# Revit family: DiLED III - Generic_3
name_source: partatom
category: Lighting Fixtures
revit_build: Autodesk Revit Architecture 2012 (Build: 20110916_2132(x64)
units: mm (PartAtom-declared; Revit-internal decimal feet)

## types (8) — shared parameters
Apparent Load = 240 VA
Assembly Code = D5020200
Cassette = Powdercoated Steel (White)
Clearance Zones Offset = 60.00 mm
Color Filter = 16777215
Dimming Lamp Color Temperature Shift = <None>
Emit Shape Visible in Rendering = No
Frame = Powdercoated Steel (White)
Glass = Lamp Glass (Opal)
Glass Thickness = 2.00 mm
Model = DiLED III
Tilt Angle = 90.00°
Transformer = Powdercoated Steel (White)
URL = www.riegens.co.uk

## per-type parameters (varying)
| type | Cassette Depth | Cassette Thickness | Cassette Width | Clearance Zones | Emit from Rectangle Length | Emit from Rectangle Width | Frame Depth | Frame Thickness | Frame Width | Glass Depth | Glass Width | Manufacturer | Photometric Web File | Transformer Offset 1 | Transformer Offset 2 | Transformer Thickness | Voids Angle |
| 300x300 - 3000K | 276.00 mm | 38.75 mm | 276.00 mm | Yes | 295.00 mm | 295.00 mm | 295.00 mm | 10.00 mm | 295.00 mm | 272.00 mm | 272.00 mm | Riegens Lighting | 8246075684_DiLEDIIIG2600x600TL152442WLED3000KCDOpal-11002.ies | 0.00 mm | 146.80 mm | 38.00 mm | 0.00° |
| 300x1200 - 3000K | 1150.00 mm | 40.20 mm | 274.00 mm | Yes | 1195.00 mm | 295.00 mm | 1195.00 mm | 9.55 mm | 295.00 mm | 1147.00 mm | 247.00 mm | Riegens Ligthing | 8246075684_DiLEDIIIG2600x600TL152442WLED3000KCDOpal-11002.ies | 275.00 mm | 275.00 mm | 36.00 mm | 33.00° |
| 625x625 - 3000K | 550.00 mm | 42.40 mm | 550.00 mm | Yes | 620.00 mm | 620.00 mm | 620.00 mm | 9.60 mm | 620.00 mm | 550.00 mm | 550.00 mm | Riegens Lighting | 8246075684_DiLEDIIIG2600x600TL152442WLED3000KCDOpal-11002.ies | 229.00 mm | 229.00 mm | 42.40 mm | 0.00° |
| 600x600 - 3000K | 550.00 mm | 42.40 mm | 550.00 mm | Yes | 595.00 mm | 595.00 mm | 595.00 mm | 9.60 mm | 595.00 mm | 549.00 mm | 549.00 mm | Riegens Ligthing | 8246075684_DiLEDIIIG2600x600TL152442WLED3000KCDOpal-11002.ies | 228.60 mm | 228.60 mm | 42.40 mm | 0.00° |
| 300x300 - 4000K | 276.00 mm | 38.75 mm | 276.00 mm | Yes | 295.00 mm | 295.00 mm | 295.00 mm | 10.00 mm | 295.00 mm | 272.00 mm | 272.00 mm | Riegens Lighting | 8246075749_DiLEDIIIG2600x600TL152442WLED4000KCDOpal-11016.ies | 0.00 mm | 146.80 mm | 38.00 mm | 0.00° |
| 300x1200 - 4000K | 1150.00 mm | 40.20 mm | 274.00 mm | Yes | 1195.00 mm | 295.00 mm | 1195.00 mm | 9.55 mm | 295.00 mm | 1147.00 mm | 247.00 mm | Riegens Lighting | 8246075749_DiLEDIIIG2600x600TL152442WLED4000KCDOpal-11016.ies | 275.00 mm | 275.00 mm | 36.00 mm | 33.00° |
| 600x600 - 4000K | 550.00 mm | 42.40 mm | 550.00 mm | No | 595.00 mm | 595.00 mm | 595.00 mm | 9.60 mm | 595.00 mm | 549.00 mm | 549.00 mm | Riegens Lighting | 8246075749_DiLEDIIIG2600x600TL152442WLED4000KCDOpal-11016.ies | 228.60 mm | 228.60 mm | 42.40 mm | 0.00° |
| 625x625 - 4000K | 550.00 mm | 42.40 mm | 550.00 mm | Yes | 620.00 mm | 620.00 mm | 620.00 mm | 9.60 mm | 620.00 mm | 550.00 mm | 550.00 mm | Riegens Lighting | 8246075749_DiLEDIIIG2600x600TL152442WLED4000KCDOpal-11016.ies | 229.00 mm | 229.00 mm | 42.40 mm | 0.00° |

## geometry (parser evidence)
native form markers: Blend x4, Sweep x8
no freeform markers — native parametric forms only
